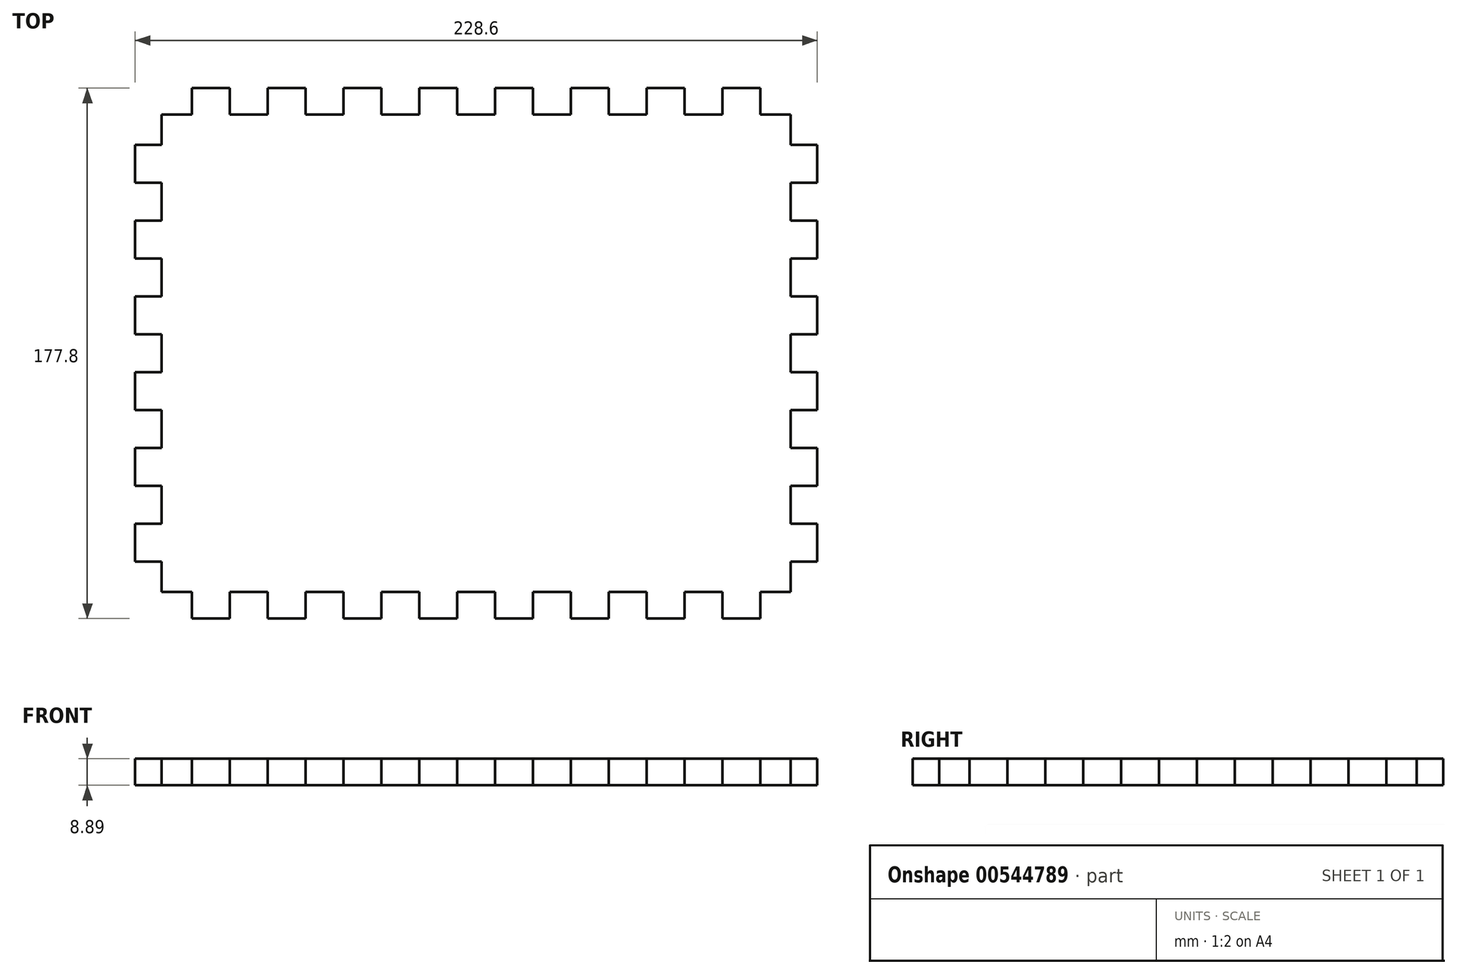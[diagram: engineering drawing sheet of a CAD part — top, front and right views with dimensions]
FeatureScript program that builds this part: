
annotation { "Feature Type Name" : "Feature", "Feature Type Description" : "" }
export const myFeature = defineFeature(function(context is Context, id is Id, definition is map)
    precondition{}
    {
        {
            var Q0;
            Q0=qCreatedBy(makeId("Top.planeOp"),FACE);
            var sketch = newSketch(context, id + "F0", { "sketchPlane" : qUnion([Q0])});
            skLineSegment(sketch, "E0.bottom", {"start": v(19.05, 0) * mm, "end": v(31.75, 0) * mm});
            skLineSegment(sketch, "E0.left", {"start": v(0, -19.05) * mm, "end": v(0, -31.75) * mm});
            skLineSegment(sketch, "E1", {"start": v(8.89, -8.9) * mm, "end": v(19.05, -8.9) * mm});
            skLineSegment(sketch, "E2", {"start": v(19.05, -8.9) * mm, "end": v(19.05, 0) * mm});
            skLineSegment(sketch, "E3", {"start": v(31.75, 0) * mm, "end": v(31.75, -8.9) * mm});
            skLineSegment(sketch, "E4", {"start": v(31.75, -8.9) * mm, "end": v(44.45, -8.9) * mm});
            skLineSegment(sketch, "E5", {"start": v(44.45, -8.9) * mm, "end": v(44.45, 0) * mm});
            skLineSegment(sketch, "E6", {"start": v(44.45, 0) * mm, "end": v(57.15, 0) * mm});
            skLineSegment(sketch, "E7", {"start": v(57.15, 0) * mm, "end": v(57.15, -8.9) * mm});
            skLineSegment(sketch, "E8", {"start": v(57.15, -8.9) * mm, "end": v(69.85, -8.9) * mm});
            skLineSegment(sketch, "E9", {"start": v(69.85, -8.9) * mm, "end": v(69.85, 0) * mm});
            skLineSegment(sketch, "E10", {"start": v(69.85, 0) * mm, "end": v(82.55, 0) * mm});
            skLineSegment(sketch, "E11", {"start": v(82.55, 0) * mm, "end": v(82.55, -8.89) * mm});
            skLineSegment(sketch, "E12", {"start": v(82.55, -8.89) * mm, "end": v(95.25, -8.89) * mm});
            skLineSegment(sketch, "E13", {"start": v(95.25, -8.89) * mm, "end": v(95.25, 0) * mm});
            skLineSegment(sketch, "E14.trimOffspring", {"start": v(95.25, 0) * mm, "end": v(107.95, 0) * mm});
            skPoint(sketch, "E15.orphan", {"position": v(0, 0) * mm});
            skLineSegment(sketch, "E16", {"start": v(107.95, 0) * mm, "end": v(107.95, -8.9) * mm});
            skLineSegment(sketch, "E17", {"start": v(107.95, -8.89) * mm, "end": v(120.65, -8.89) * mm});
            skLineSegment(sketch, "E18", {"start": v(120.65, -8.9) * mm, "end": v(120.65, 0) * mm});
            skLineSegment(sketch, "E19", {"start": v(120.65, 0) * mm, "end": v(133.35, 0) * mm});
            skLineSegment(sketch, "E20", {"start": v(133.35, 0) * mm, "end": v(133.35, -8.9) * mm});
            skLineSegment(sketch, "E21", {"start": v(133.35, -8.89) * mm, "end": v(146.05, -8.89) * mm});
            skLineSegment(sketch, "E22", {"start": v(146.05, -8.89) * mm, "end": v(146.05, 0) * mm});
            skLineSegment(sketch, "E23", {"start": v(146.05, 0) * mm, "end": v(158.75, 0) * mm});
            skLineSegment(sketch, "E24", {"start": v(158.75, 0) * mm, "end": v(158.75, -8.89) * mm});
            skLineSegment(sketch, "E25", {"start": v(158.75, -8.89) * mm, "end": v(171.45, -8.89) * mm});
            skLineSegment(sketch, "E26", {"start": v(171.45, -8.89) * mm, "end": v(171.45, 0) * mm});
            skLineSegment(sketch, "E27", {"start": v(171.45, 0) * mm, "end": v(184.15, 0) * mm});
            skLineSegment(sketch, "E28", {"start": v(184.15, 0) * mm, "end": v(184.15, -8.89) * mm});
            skLineSegment(sketch, "E29", {"start": v(184.15, -8.89) * mm, "end": v(196.85, -8.89) * mm});
            skLineSegment(sketch, "E30", {"start": v(196.85, -8.89) * mm, "end": v(196.85, 0) * mm});
            skLineSegment(sketch, "E31", {"start": v(196.85, 0) * mm, "end": v(209.55, 0) * mm});
            skLineSegment(sketch, "E32", {"start": v(209.55, 0) * mm, "end": v(209.55, -8.89) * mm});
            skPoint(sketch, "E33.orphan", {"position": v(228.6, 0) * mm});
            skLineSegment(sketch, "E34", {"start": v(8.89, -8.9) * mm, "end": v(8.89, -19.05) * mm});
            skLineSegment(sketch, "E35", {"start": v(8.9, -19.05) * mm, "end": v(0, -19.05) * mm});
            skLineSegment(sketch, "E36", {"start": v(0, -31.75) * mm, "end": v(8.9, -31.75) * mm});
            skLineSegment(sketch, "E37", {"start": v(8.89, -31.75) * mm, "end": v(8.89, -44.45) * mm});
            skLineSegment(sketch, "E38", {"start": v(8.9, -44.45) * mm, "end": v(0, -44.45) * mm});
            skLineSegment(sketch, "E39", {"start": v(0, -44.45) * mm, "end": v(0, -57.15) * mm});
            skLineSegment(sketch, "E40", {"start": v(0, -57.15) * mm, "end": v(8.9, -57.15) * mm});
            skLineSegment(sketch, "E41", {"start": v(8.89, -57.15) * mm, "end": v(8.89, -69.85) * mm});
            skLineSegment(sketch, "E42", {"start": v(8.9, -69.85) * mm, "end": v(0, -69.85) * mm});
            skLineSegment(sketch, "E43", {"start": v(0, -69.85) * mm, "end": v(0, -82.55) * mm});
            skLineSegment(sketch, "E44", {"start": v(0, -82.55) * mm, "end": v(8.9, -82.55) * mm});
            skLineSegment(sketch, "E45", {"start": v(8.89, -82.55) * mm, "end": v(8.89, -95.25) * mm});
            skLineSegment(sketch, "E46", {"start": v(8.9, -95.25) * mm, "end": v(0, -95.25) * mm});
            skLineSegment(sketch, "E47.trimOffspring", {"start": v(0, -95.25) * mm, "end": v(0, -107.95) * mm});
            skLineSegment(sketch, "E48", {"start": v(0, -107.95) * mm, "end": v(8.9, -107.95) * mm});
            skLineSegment(sketch, "E49", {"start": v(8.9, -107.95) * mm, "end": v(8.9, -120.65) * mm});
            skLineSegment(sketch, "E50", {"start": v(8.9, -120.65) * mm, "end": v(0, -120.65) * mm});
            skLineSegment(sketch, "E51", {"start": v(0, -120.65) * mm, "end": v(0, -133.35) * mm});
            skLineSegment(sketch, "E52", {"start": v(0, -133.35) * mm, "end": v(8.9, -133.35) * mm});
            skPoint(sketch, "E53.orphan", {"position": v(0, -177.8) * mm});
            skLineSegment(sketch, "E54", {"start": v(8.9, -133.35) * mm, "end": v(8.9, -146.05) * mm});
            skLineSegment(sketch, "E55", {"start": v(8.9, -146.05) * mm, "end": v(0, -146.05) * mm});
            skLineSegment(sketch, "E56", {"start": v(0, -146.05) * mm, "end": v(0, -158.75) * mm});
            skLineSegment(sketch, "E57", {"start": v(0, -158.75) * mm, "end": v(8.9, -158.75) * mm});
            skLineSegment(sketch, "E58", {"start": v(8.9, -158.75) * mm, "end": v(8.9, -168.9) * mm});
            skLineSegment(sketch, "E59", {"start": v(8.9, -168.9) * mm, "end": v(19.05, -168.9) * mm});
            skLineSegment(sketch, "E60", {"start": v(19.05, -168.9) * mm, "end": v(19.05, -177.8) * mm});
            skLineSegment(sketch, "E61", {"start": v(114.3, -8.89) * mm, "end": v(114.3, -63.74) * mm, "construction": true});
            skLineSegment(sketch, "E62", {"start": v(8.89, -88.9) * mm, "end": v(67.56, -88.9) * mm, "construction": true});
            skLineSegment(sketch, "E63.MirrorCS", {"start": v(219.71, -8.9) * mm, "end": v(219.71, -19.05) * mm});
            skLineSegment(sketch, "E64.MirrorCS", {"start": v(219.71, -19.05) * mm, "end": v(228.6, -19.05) * mm});
            skLineSegment(sketch, "E65.MirrorCS", {"start": v(228.6, -19.05) * mm, "end": v(228.6, -31.75) * mm});
            skLineSegment(sketch, "E66.MirrorCS", {"start": v(228.6, -31.75) * mm, "end": v(219.7, -31.75) * mm});
            skLineSegment(sketch, "E67.MirrorCS", {"start": v(219.71, -31.75) * mm, "end": v(219.71, -44.45) * mm});
            skLineSegment(sketch, "E68.MirrorCS", {"start": v(219.7, -44.45) * mm, "end": v(228.6, -44.45) * mm});
            skLineSegment(sketch, "E69.MirrorCS", {"start": v(228.6, -44.45) * mm, "end": v(228.6, -57.15) * mm});
            skLineSegment(sketch, "E70.MirrorCS", {"start": v(228.6, -57.15) * mm, "end": v(219.7, -57.15) * mm});
            skLineSegment(sketch, "E71.MirrorCS", {"start": v(219.71, -57.15) * mm, "end": v(219.71, -69.85) * mm});
            skLineSegment(sketch, "E72.MirrorCS", {"start": v(219.7, -69.85) * mm, "end": v(228.6, -69.85) * mm});
            skLineSegment(sketch, "E73.MirrorCS", {"start": v(228.6, -69.85) * mm, "end": v(228.6, -82.55) * mm});
            skLineSegment(sketch, "E74.MirrorCS", {"start": v(228.6, -82.55) * mm, "end": v(219.7, -82.55) * mm});
            skLineSegment(sketch, "E75.MirrorCS", {"start": v(219.71, -82.55) * mm, "end": v(219.71, -95.25) * mm});
            skLineSegment(sketch, "E76.MirrorCS", {"start": v(219.7, -95.25) * mm, "end": v(228.6, -95.25) * mm});
            skLineSegment(sketch, "E77.MirrorCS", {"start": v(228.6, -95.25) * mm, "end": v(228.6, -107.95) * mm});
            skLineSegment(sketch, "E78.MirrorCS", {"start": v(228.6, -107.95) * mm, "end": v(219.71, -107.95) * mm});
            skLineSegment(sketch, "E79.MirrorCS", {"start": v(219.71, -107.95) * mm, "end": v(219.71, -120.65) * mm});
            skLineSegment(sketch, "E80.MirrorCS", {"start": v(219.71, -120.65) * mm, "end": v(228.6, -120.65) * mm});
            skLineSegment(sketch, "E81.MirrorCS", {"start": v(228.6, -120.65) * mm, "end": v(228.6, -133.35) * mm});
            skLineSegment(sketch, "E82.MirrorCS", {"start": v(228.6, -133.35) * mm, "end": v(219.71, -133.35) * mm});
            skLineSegment(sketch, "E83.MirrorCS", {"start": v(219.71, -133.35) * mm, "end": v(219.71, -146.05) * mm});
            skLineSegment(sketch, "E84.MirrorCS", {"start": v(219.71, -146.05) * mm, "end": v(228.6, -146.05) * mm});
            skLineSegment(sketch, "E85.MirrorCS", {"start": v(228.6, -146.05) * mm, "end": v(228.6, -158.75) * mm});
            skLineSegment(sketch, "E86.MirrorCS", {"start": v(219.71, -158.75) * mm, "end": v(219.71, -168.9) * mm});
            skLineSegment(sketch, "E87.MirrorCS", {"start": v(219.71, -168.9) * mm, "end": v(209.55, -168.9) * mm});
            skLineSegment(sketch, "E88.MirrorCS", {"start": v(209.55, -168.9) * mm, "end": v(209.55, -177.8) * mm});
            skLineSegment(sketch, "E89.MirrorCS", {"start": v(228.6, -158.75) * mm, "end": v(219.71, -158.75) * mm});
            skLineSegment(sketch, "E90", {"start": v(209.55, -8.9) * mm, "end": v(219.71, -8.89) * mm});
            skLineSegment(sketch, "E91.MirrorCS", {"start": v(19.05, -177.8) * mm, "end": v(31.75, -177.8) * mm});
            skLineSegment(sketch, "E92.MirrorCS", {"start": v(31.75, -177.8) * mm, "end": v(31.75, -168.9) * mm});
            skLineSegment(sketch, "E93.MirrorCS", {"start": v(31.75, -168.9) * mm, "end": v(44.45, -168.9) * mm});
            skLineSegment(sketch, "E94.MirrorCS", {"start": v(44.45, -168.9) * mm, "end": v(44.45, -177.8) * mm});
            skLineSegment(sketch, "E95.MirrorCS", {"start": v(44.45, -177.8) * mm, "end": v(57.15, -177.8) * mm});
            skLineSegment(sketch, "E96.MirrorCS", {"start": v(57.15, -177.8) * mm, "end": v(57.15, -168.9) * mm});
            skLineSegment(sketch, "E97.MirrorCS", {"start": v(57.15, -168.9) * mm, "end": v(69.85, -168.9) * mm});
            skLineSegment(sketch, "E98.MirrorCS", {"start": v(69.85, -168.91) * mm, "end": v(69.85, -177.8) * mm});
            skLineSegment(sketch, "E99.MirrorCS", {"start": v(69.85, -177.8) * mm, "end": v(82.55, -177.8) * mm});
            skLineSegment(sketch, "E100.MirrorCS", {"start": v(82.55, -177.8) * mm, "end": v(82.55, -168.91) * mm});
            skLineSegment(sketch, "E101.MirrorCS", {"start": v(82.55, -168.91) * mm, "end": v(95.25, -168.91) * mm});
            skLineSegment(sketch, "E102.MirrorCS", {"start": v(95.25, -168.91) * mm, "end": v(95.25, -177.8) * mm});
            skLineSegment(sketch, "E103.MirrorCS", {"start": v(95.25, -177.8) * mm, "end": v(107.95, -177.8) * mm});
            skLineSegment(sketch, "E104.MirrorCS", {"start": v(107.95, -177.8) * mm, "end": v(107.95, -168.9) * mm});
            skLineSegment(sketch, "E105.MirrorCS", {"start": v(107.95, -168.91) * mm, "end": v(120.65, -168.91) * mm});
            skLineSegment(sketch, "E106.MirrorCS", {"start": v(120.65, -168.9) * mm, "end": v(120.65, -177.8) * mm});
            skLineSegment(sketch, "E107.MirrorCS", {"start": v(120.65, -177.8) * mm, "end": v(133.35, -177.8) * mm});
            skLineSegment(sketch, "E108.MirrorCS", {"start": v(133.35, -177.8) * mm, "end": v(133.35, -168.9) * mm});
            skLineSegment(sketch, "E109.MirrorCS", {"start": v(133.35, -168.91) * mm, "end": v(146.05, -168.91) * mm});
            skLineSegment(sketch, "E110.MirrorCS", {"start": v(146.05, -168.9) * mm, "end": v(146.05, -177.8) * mm});
            skLineSegment(sketch, "E111.MirrorCS", {"start": v(146.05, -177.8) * mm, "end": v(158.75, -177.8) * mm});
            skLineSegment(sketch, "E112.MirrorCS", {"start": v(158.75, -177.8) * mm, "end": v(158.75, -168.9) * mm});
            skLineSegment(sketch, "E113.MirrorCS", {"start": v(158.75, -168.91) * mm, "end": v(171.45, -168.91) * mm});
            skLineSegment(sketch, "E114.MirrorCS", {"start": v(171.45, -168.91) * mm, "end": v(171.45, -177.8) * mm});
            skLineSegment(sketch, "E115.MirrorCS", {"start": v(171.45, -177.8) * mm, "end": v(184.15, -177.8) * mm});
            skLineSegment(sketch, "E116.MirrorCS", {"start": v(184.15, -177.8) * mm, "end": v(184.15, -168.9) * mm});
            skLineSegment(sketch, "E117.MirrorCS", {"start": v(184.15, -168.91) * mm, "end": v(196.85, -168.91) * mm});
            skLineSegment(sketch, "E118.MirrorCS", {"start": v(196.85, -168.91) * mm, "end": v(196.85, -177.8) * mm});
            skLineSegment(sketch, "E119.MirrorCS", {"start": v(196.85, -177.8) * mm, "end": v(209.55, -177.8) * mm});
            skSolve(sketch);
        }
        {
            var Q0;
            Q0=makeQuery(id+"F0.imprint","IMPRINT",FACE,{"disambiguationData":[TD([[makeQuery(id+"F0.imprint","IMPRINT",EDGE,{"derivedFrom":sQuery(id+"F0.wireOp",EDGE,"E1")}),-1.0]])]});
            extrude(context, id + "F1", {"entities" : qUnion([Q0]), "depth" : 8.9 * mm, "offsetDistance" : 25.4 * mm});
        }
    });
